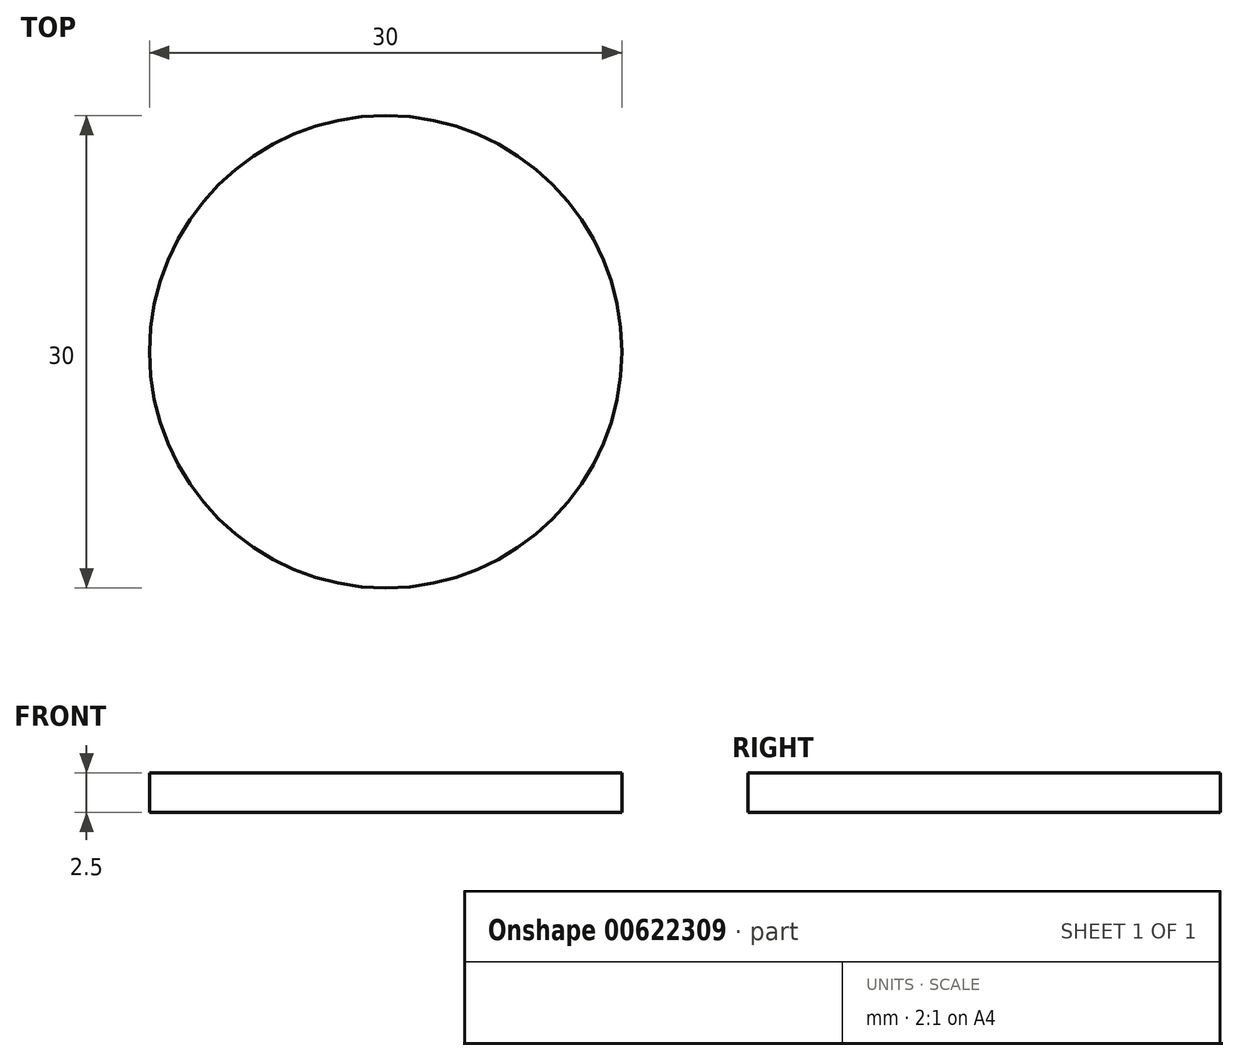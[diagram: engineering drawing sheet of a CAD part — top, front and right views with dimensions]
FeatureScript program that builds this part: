
annotation { "Feature Type Name" : "Feature", "Feature Type Description" : "" }
export const myFeature = defineFeature(function(context is Context, id is Id, definition is map)
    precondition{}
    {
        {
            assignVariable(context, id + "F0", {"name" : "d", "anyValue" : 2.5});
        }
        {
            var Q0;
            Q0=qCreatedBy(makeId("Top.planeOp"),FACE);
            var sketch = newSketch(context, id + "F1", { "sketchPlane" : qUnion([Q0])});
            skCircle(sketch, "E0", {"center": v(0, 0) * mm, "radius": 15 * mm});
            skSolve(sketch);
        }
        {
            var Q0;
            Q0=makeQuery(id+"F1.imprint","IMPRINT",FACE,{"disambiguationData":[TD([[makeQuery(id+"F1.imprint","IMPRINT",EDGE,{"derivedFrom":sQuery(id+"F1.wireOp",EDGE,"E0")}),1.0]])]});
            extrude(context, id + "F2", {"entities" : qUnion([Q0]), "depth" : (getVariable(context, 'd')) * mm, "offsetDistance" : 25 * mm});
        }
    });
